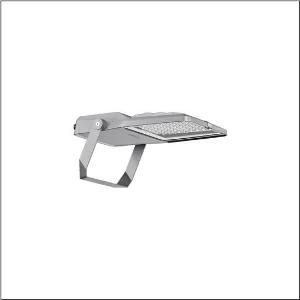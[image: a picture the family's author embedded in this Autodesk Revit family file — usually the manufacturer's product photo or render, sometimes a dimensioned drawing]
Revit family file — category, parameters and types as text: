
# Revit family: floodlight_fl_21_iq_mini___pl52_5xa7772c5d1a_6522
name_source: partatom
category: Lighting Fixtures
units: mm (PartAtom-declared; Revit-internal decimal feet)

## family parameters
Cut with Voids When Loaded = No
Host = Face
Light Source = No
Part Type = Normal
Room Calculation Point = No
Round Connector Dimension = Use Diameter
Shared = No

## types (1)
- --- (1 x LED, 11390 lm, 87.2 W, 4000K)
    Apparent Load = 87 VA
    CIE Flux Codes = 26 60 98 100 100
    Color Rendering = 80
    Color Temperature = 4000K
    Default Elevation = 1800 mm
    Description = Floodlight FL 21 iQ mini, floodlight, primary light control with lens, of PMMA, primary optical cover: protective disc, of toughened safety glass, transparent, light distribution: PL52, light emission: direct distribution, installation type: surface-mounted, lamps: LED, High Power LED, rated values: 11.390lm | 87,2W | 130,6lm/W (begin service life); end service life: 11.390lm | 92,1W; at 50% lumin. flux: 5.695lm | 40,1W | 142lm/W, colour temperature: 4000K, colour rendering: CRI > 80, light colour: 840, light setting 1 begin service life: 100% | 11.390lm | 87,2W | 130,6lm/W | 4.000K, light setting 1 end service life: 92,1W, further light settings possible, control: Street-Remote, Auto-Match, Temp-Guard, Night-Set, Smart-Wire, Desk-Remote (wireless, voltage-free reading and setting of iQ features in the workshop via application-optimized NFC function/RFID function), optimised constant luminous flux control (CLO 2.0), pre-setting: linear dimming characteristic, with terminal, 6-pole, mains connection: 220..240V, AC, 50/60Hz, luminaire housing, of diecast aluminium, powder-coated, SITECO metallic grey (DB 702S), corrosivity category C5 mid according to DIN EN ISO 12944suitable for swimming poolschlorine-resistant, sealing non-destructively replaceable, mounting bracket, of steel, galvanised, powder-coated, SITECO metallic grey (DB 702S), protection rating (complete): IP66, insulation class (complete): insulation class II (safety insulation), certification: CE, ENEC, VDE, protection symbol: D, impact resistance: IK08, permissible operating ambient temperature: -40..+40°C, permissible operating ambient temperature for outdoor applications: -40..+50°C, standard: DIN EN 12944, LABS conformity tested according to VDMA 24364:2018-05, packaging unit: 1 piece

Light Distribution: PL52
    Height = 70 mm
    Lamp = 1 x LED
    Lamp Light Flux = 11390 lm
    Lamp Power = 87.2 W
    Lamp count = 1
    Length = 485 mm
    Luminous efficacy = 131 lm/W
    Manufacturer = Siteco
    ModVariant = No
    Model = 5XA7772C5D1A
    Mounting Place = Pole
    Mounting Type = Pole annexe
    Number of Poles = 1
    OnlyDefault = Yes
    Power Factor = 1
    Product Name = Floodlight FL 21 iQ mini | PL52
    Product group = floodlight | pylon annexe
    ProductGroupID = 6201
    Protection Class = Protection class II
    Protection Degree = IP 66
    RLX_Detail_Level = 1
    RLX_Emergency_Light_Flux = 0 lm
    RLX_Emergency_Type = 0
    RLX_Emergency_Type_DB = No
    RlxData = <blob elided: 96525 chars, md5=bc872c1b>
    Socket = socket
    Standby Power = 0 W
    System Light Flux = 11390 lm
    System Power = 87 W
    Type Comments = factory setting: luminous flux: 100 % | dim-lin: 254 | 456 mA
    Type Image = l_1006845.jpg
    URL = http://relux.com
    VarID = @adj_165149
    Voltage = 0 V
    Weight = 0.00 kg
    Width = 337 mm

## geometry (parser evidence)
native form markers: Blend x4, Sweep x12
no freeform markers — native parametric forms only
